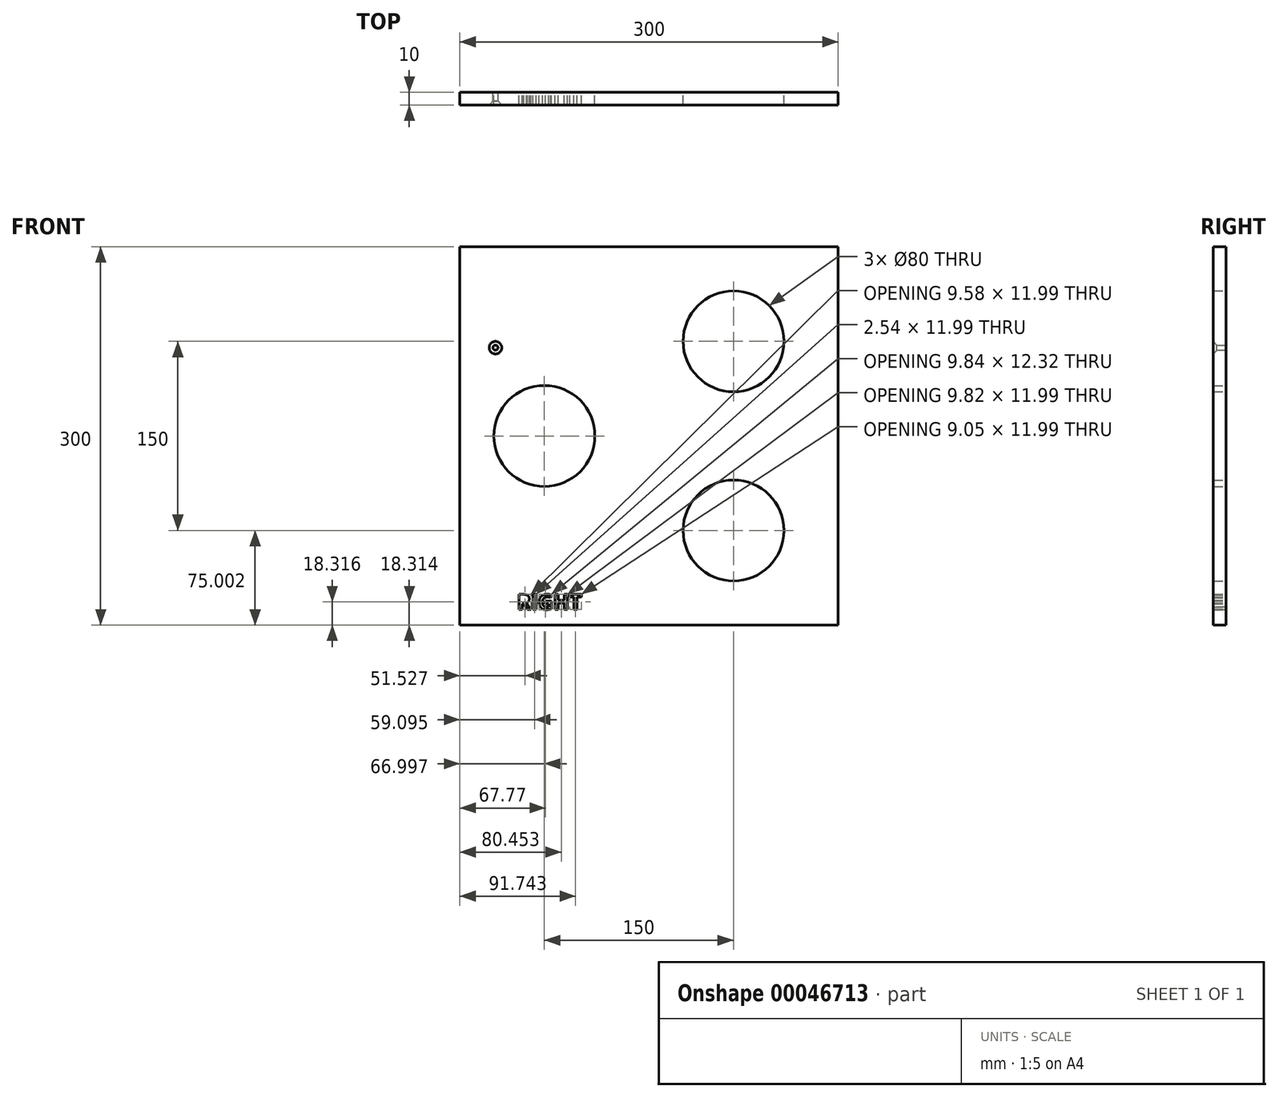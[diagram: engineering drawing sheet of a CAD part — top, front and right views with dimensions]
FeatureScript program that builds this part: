
annotation { "Feature Type Name" : "Feature", "Feature Type Description" : "" }
export const myFeature = defineFeature(function(context is Context, id is Id, definition is map)
    precondition{}
    {
        {
            var Q0;
            Q0=qCreatedBy(makeId("Front.planeOp"),FACE);
            var sketch = newSketch(context, id + "F0", { "sketchPlane" : qUnion([Q0])});
            skLineSegment(sketch, "E0.bottom", {"start": v(-161.01, 139.55) * mm, "end": v(138.99, 139.55) * mm});
            skLineSegment(sketch, "E0.top", {"start": v(-161.01, -160.45) * mm, "end": v(138.99, -160.45) * mm});
            skLineSegment(sketch, "E0.left", {"start": v(-161.01, 139.55) * mm, "end": v(-161.01, -160.45) * mm});
            skLineSegment(sketch, "E0.right", {"start": v(138.99, 139.55) * mm, "end": v(138.99, -160.45) * mm});
            skCircle(sketch, "E1", {"center": v(55.99, 64.55) * mm, "radius": 40 * mm});
            skCircle(sketch, "E2", {"center": v(-94.01, -10.45) * mm, "radius": 40 * mm});
            skCircle(sketch, "E3", {"center": v(55.99, -85.45) * mm, "radius": 40 * mm});
            skCircle(sketch, "E4", {"center": v(-132.8, 59.55) * mm, "radius": 2 * mm});
            skLineSegment(sketch, "E5", {"start": v(-27.01, 175.9) * mm, "end": v(-27.01, -182.73) * mm, "construction": true});
            skText(sketch, "E6", { "text": "RIGHT", "fontName": "OpenSans-Bold.ttf"});
            const initialGuessF0  = {"E6": [-0.11578, -0.14813, 1, 0, 0.01209]};
            skSetInitialGuess(sketch, initialGuessF0);
            skSolve(sketch);
        }
        {
            var Q0;
            Q0=makeQuery(id+"F0.imprint","IMPRINT",FACE,{"disambiguationData":[TD([[makeQuery(id+"F0.imprint","IMPRINT",EDGE,{"derivedFrom":sQuery(id+"F0.wireOp",EDGE,"E0.bottom")}),-1.0]])]});
            extrude(context, id + "F1", {"entities" : qUnion([Q0]), "depth" : 10 * mm});
        }
        {
            var Q0;
            Q0=makeQuery(id+"F1.opExtrude","CAP_EDGE",EDGE,{"disambiguationData":[OSD([sQuery(id+"F0.wireOp",EDGE,"E4")])],"isStart":false});
            chamfer(context, id + "F2", {"entities" : qUnion([Q0]), "width" : 3 * mm, "tangentPropagation" : true});
        }
    });
